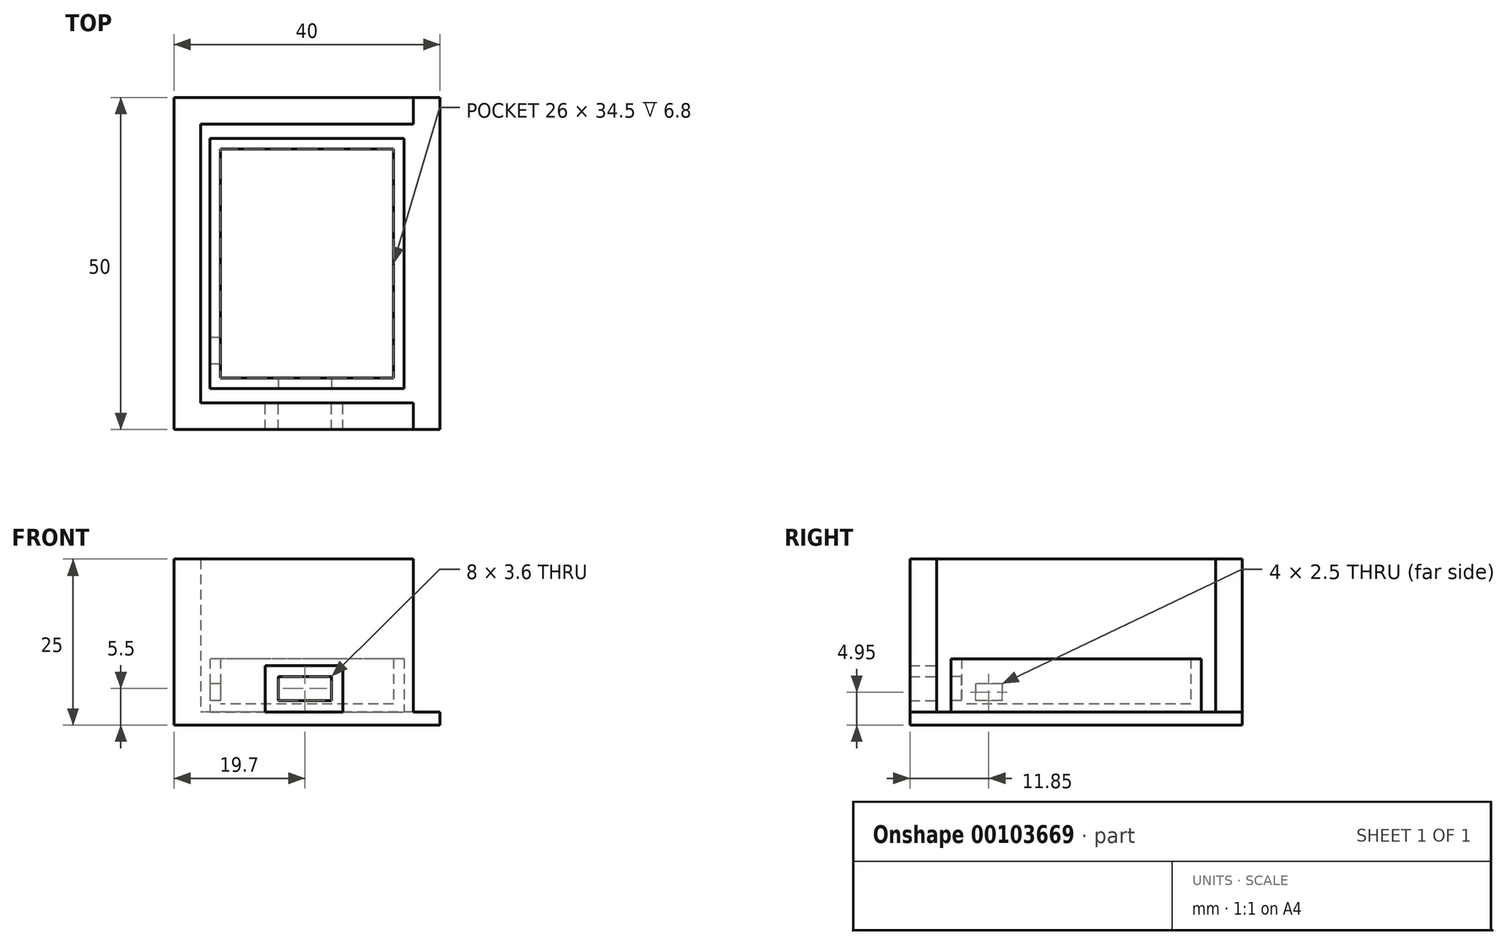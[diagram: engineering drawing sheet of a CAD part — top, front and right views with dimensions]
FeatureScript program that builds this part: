
annotation { "Feature Type Name" : "Feature", "Feature Type Description" : "" }
export const myFeature = defineFeature(function(context is Context, id is Id, definition is map)
    precondition{}
    {
        {
            var Q0;
            Q0=qCreatedBy(makeId("Top.planeOp"),FACE);
            var sketch = newSketch(context, id + "F0", { "sketchPlane" : qUnion([Q0])});
            skLineSegment(sketch, "E0.bottom", {"start": v(14.6, 18.85) * mm, "end": v(-14.6, 18.85) * mm});
            skLineSegment(sketch, "E0.top", {"start": v(14.6, -18.85) * mm, "end": v(-14.6, -18.85) * mm});
            skLineSegment(sketch, "E0.left", {"start": v(14.6, 18.85) * mm, "end": v(14.6, -18.85) * mm});
            skLineSegment(sketch, "E0.right", {"start": v(-14.6, 18.85) * mm, "end": v(-14.6, -18.85) * mm});
            skPoint(sketch, "E0.middle", {"position": v(0, 0) * mm});
            skSolve(sketch);
        }
        {
            var Q0;
            Q0=makeQuery(id+"F0.imprint","IMPRINT",FACE,{"disambiguationData":[TD([[makeQuery(id+"F0.imprint","IMPRINT",EDGE,{"derivedFrom":sQuery(id+"F0.wireOp",EDGE,"E0.bottom")}),1.0]])]});
            extrude(context, id + "F1", {"entities" : qUnion([Q0]), "depth" : 10 * mm});
        }
        {
            var Q0;
            Q0=makeQuery(id+"F1.opExtrude","CAP_FACE",FACE,{"disambiguationData":[OSD([sQuery(id+"F0.wireOp",EDGE,"E0.bottom"),sQuery(id+"F0.wireOp",EDGE,"E0.top"),sQuery(id+"F0.wireOp",EDGE,"E0.left"),sQuery(id+"F0.wireOp",EDGE,"E0.right")])],"isStart":false});
            shell(context, id + "F2", {"entities" : qUnion([Q0]), "thickness" : 1.6 * mm});
        }
        {
            var Q0;
            Q0=makeQuery(id+"F1.opExtrude","SWEPT_FACE",FACE,{"disambiguationData":[OSD([sQuery(id+"F0.wireOp",EDGE,"E0.top")])]});
            var sketch = newSketch(context, id + "F3", { "sketchPlane" : qUnion([Q0])});
            skLineSegment(sketch, "E1.bottom", {"start": v(-4.3, 7.3) * mm, "end": v(3.7, 7.3) * mm});
            skLineSegment(sketch, "E1.top", {"start": v(-4.3, 3.7) * mm, "end": v(3.7, 3.7) * mm});
            skLineSegment(sketch, "E1.left", {"start": v(-4.3, 7.3) * mm, "end": v(-4.3, 3.7) * mm});
            skLineSegment(sketch, "E1.right", {"start": v(3.7, 7.3) * mm, "end": v(3.7, 3.7) * mm});
            skPoint(sketch, "E2.endSnap0", {"position": v(0, 0) * mm});
            skPoint(sketch, "E3", {"position": v(-0.3, 7.3) * mm});
            skLineSegment(sketch, "E4", {"start": v(-2.82, 0) * mm, "end": v(-2.82, 3.7) * mm, "construction": true});
            skLineSegment(sketch, "E5", {"start": v(-4.3, 3.7) * mm, "end": v(-14.6, 3.7) * mm, "construction": true});
            skSolve(sketch);
        }
        {
            var Q0;
            Q0=makeQuery(id+"F3.imprint","IMPRINT",FACE,{"disambiguationData":[TD([[makeQuery(id+"F3.imprint","IMPRINT",EDGE,{"derivedFrom":sQuery(id+"F3.wireOp",EDGE,"E1.bottom")}),-1.0]])]});
            var Q1;
            Q1=makeQuery(id+"F2.opShell","OFFSET_FACE",FACE,{"disambiguationData":[OSD([sQuery(id+"F0.wireOp",EDGE,"E0.top")])]});
            extrude(context, id + "F4", {"entities" : qUnion([Q0]), "operationType" : NewBodyOperationType.REMOVE, "endBound" : BoundingType.UP_TO_SURFACE, "oppositeDirection" : true, "endBoundEntityFace" : qUnion([Q1]), "depth" : 25 * mm});
        }
        {
            var Q0;
            Q0=makeQuery(id+"F1.opExtrude","SWEPT_FACE",FACE,{"disambiguationData":[OSD([sQuery(id+"F0.wireOp",EDGE,"E0.right")])]});
            var sketch = newSketch(context, id + "F5", { "sketchPlane" : qUnion([Q0])});
            skLineSegment(sketch, "E6.bottom", {"start": v(11.15, 6.2) * mm, "end": v(15.15, 6.2) * mm});
            skLineSegment(sketch, "E6.top", {"start": v(11.15, 3.7) * mm, "end": v(15.15, 3.7) * mm});
            skLineSegment(sketch, "E6.left", {"start": v(11.15, 6.2) * mm, "end": v(11.15, 3.7) * mm});
            skLineSegment(sketch, "E6.right", {"start": v(15.15, 6.2) * mm, "end": v(15.15, 3.7) * mm});
            skLineSegment(sketch, "E7", {"start": v(15.15, 3.7) * mm, "end": v(18.85, 3.7) * mm, "construction": true});
            skLineSegment(sketch, "E8", {"start": v(15.15, 3.7) * mm, "end": v(15.15, 0) * mm, "construction": true});
            skSolve(sketch);
        }
        {
            var Q0;
            Q0=makeQuery(id+"F5.imprint","IMPRINT",FACE,{"disambiguationData":[TD([[makeQuery(id+"F5.imprint","IMPRINT",EDGE,{"derivedFrom":sQuery(id+"F5.wireOp",EDGE,"E6.bottom")}),-1.0]])]});
            var Q1;
            Q1=makeQuery(id+"F2.opShell","OFFSET_FACE",FACE,{"disambiguationData":[OSD([sQuery(id+"F0.wireOp",EDGE,"E0.right")])]});
            extrude(context, id + "F6", {"entities" : qUnion([Q0]), "operationType" : NewBodyOperationType.REMOVE, "endBound" : BoundingType.UP_TO_SURFACE, "oppositeDirection" : true, "endBoundEntityFace" : qUnion([Q1]), "depth" : 25 * mm});
        }
        {
            var Q0;
            Q0=makeQuery(id+"F2.opShell","OFFSET_FACE",FACE,{"disambiguationData":[OSD([sQuery(id+"F0.wireOp",EDGE,"E0.bottom"),sQuery(id+"F0.wireOp",EDGE,"E0.top"),sQuery(id+"F0.wireOp",EDGE,"E0.left"),sQuery(id+"F0.wireOp",EDGE,"E0.right")])]});
            var sketch = newSketch(context, id + "F7", { "sketchPlane" : qUnion([Q0])});
            skLineSegment(sketch, "E9.bottom", {"start": v(-13, 17.25) * mm, "end": v(13, 17.25) * mm});
            skLineSegment(sketch, "E9.top", {"start": v(-13, -17.25) * mm, "end": v(13, -17.25) * mm});
            skLineSegment(sketch, "E9.left", {"start": v(-13, 17.25) * mm, "end": v(-13, -17.25) * mm});
            skLineSegment(sketch, "E9.right", {"start": v(13, 17.25) * mm, "end": v(13, -17.25) * mm});
            skSolve(sketch);
        }
        {
            var Q0;
            Q0=makeQuery(id+"F7.imprint","IMPRINT",FACE,{"disambiguationData":[TD([[makeQuery(id+"F7.imprint","IMPRINT",EDGE,{"derivedFrom":sQuery(id+"F7.wireOp",EDGE,"E9.bottom")}),1.0]])]});
            extrude(context, id + "F8", {"entities" : qUnion([Q0]), "operationType" : NewBodyOperationType.ADD, "depth" : 1.6 * mm});
        }
        {
            var Q0;
            Q0=makeQuery(id+"F1.opExtrude","CAP_FACE",FACE,{"disambiguationData":[OSD([sQuery(id+"F0.wireOp",EDGE,"E0.bottom"),sQuery(id+"F0.wireOp",EDGE,"E0.top"),sQuery(id+"F0.wireOp",EDGE,"E0.left"),sQuery(id+"F0.wireOp",EDGE,"E0.right")])],"isStart":true});
            var sketch = newSketch(context, id + "F9", { "sketchPlane" : qUnion([Q0])});
            skLineSegment(sketch, "E10.bottom", {"start": v(-20, -25) * mm, "end": v(20, -25) * mm});
            skLineSegment(sketch, "E10.top", {"start": v(-20, 25) * mm, "end": v(20, 25) * mm});
            skLineSegment(sketch, "E10.left", {"start": v(-20, -25) * mm, "end": v(-20, 25) * mm});
            skLineSegment(sketch, "E10.right", {"start": v(20, -25) * mm, "end": v(20, 25) * mm});
            skPoint(sketch, "E10.middle", {"position": v(0, 0) * mm});
            skLineSegment(sketch, "E11.bottom", {"start": v(20, 25) * mm, "end": v(16, 25) * mm});
            skLineSegment(sketch, "E11.top", {"start": v(20, -25) * mm, "end": v(16, -25) * mm});
            skLineSegment(sketch, "E11.left", {"start": v(20, 25) * mm, "end": v(20, -25) * mm});
            skLineSegment(sketch, "E11.right", {"start": v(16, 25) * mm, "end": v(16, -25) * mm});
            skLineSegment(sketch, "E12.bottom", {"start": v(-20, -25) * mm, "end": v(-16, -25) * mm});
            skLineSegment(sketch, "E12.top", {"start": v(-20, 25) * mm, "end": v(-16, 25) * mm});
            skLineSegment(sketch, "E12.right", {"start": v(-16, -25) * mm, "end": v(-16, 25) * mm});
            skLineSegment(sketch, "E13.top", {"start": v(-20, -21) * mm, "end": v(20, -21) * mm});
            skLineSegment(sketch, "E13.left", {"start": v(-20, -25) * mm, "end": v(-20, -21) * mm});
            skLineSegment(sketch, "E13.right", {"start": v(20, -25) * mm, "end": v(20, -21) * mm});
            skLineSegment(sketch, "E14.top", {"start": v(-20, 21) * mm, "end": v(20, 21) * mm});
            skLineSegment(sketch, "E14.left", {"start": v(-20, 25) * mm, "end": v(-20, 21) * mm});
            skLineSegment(sketch, "E14.right", {"start": v(20, 25) * mm, "end": v(20, 21) * mm});
            skSolve(sketch);
        }
        {
            var Q0;
            {var subQ0=sQuery(id+"F9.wireOp",EDGE,"E10.bottom");var subQ1=sQuery(id+"F9.wireOp",EDGE,"E11.right");var subQ2=makeQuery(id+"F9.imprint","INTERSECT",VERTEX,{"derivedFrom":[subQ1,subQ0]});Q0=makeQuery(id+"F9.imprint","IMPRINT",FACE,{"disambiguationData":[TD([[makeQuery(id+"F9.imprint","IMPRINT",EDGE,{"disambiguationData":[TD([[subQ2,1.0]])],"derivedFrom":subQ1}),-1.0]])]});}
            var Q1;
            {var subQ5=sQuery(id+"F9.wireOp",EDGE,"E13.left");Q1=makeQuery(id+"F9.imprint","IMPRINT",FACE,{"disambiguationData":[TD([[makeQuery(id+"F9.imprint","IMPRINT",EDGE,{"derivedFrom":subQ5}),-1.0]])]});}
            var Q2;
            {var subQ5=sQuery(id+"F9.wireOp",EDGE,"E13.right");Q2=makeQuery(id+"F9.imprint","IMPRINT",FACE,{"disambiguationData":[TD([[makeQuery(id+"F9.imprint","IMPRINT",EDGE,{"derivedFrom":subQ5}),1.0]])]});}
            var Q3;
            {var subQ0=sQuery(id+"F9.wireOp",EDGE,"E11.left");Q3=makeQuery(id+"F9.imprint","IMPRINT",FACE,{"disambiguationData":[TD([[makeQuery(id+"F9.imprint","IMPRINT",EDGE,{"derivedFrom":subQ0}),-1.0]])]});}
            var Q4;
            {var subQ5=sQuery(id+"F9.wireOp",EDGE,"E14.right");Q4=makeQuery(id+"F9.imprint","IMPRINT",FACE,{"disambiguationData":[TD([[makeQuery(id+"F9.imprint","IMPRINT",EDGE,{"derivedFrom":subQ5}),-1.0]])]});}
            var Q5;
            {var subQ0=sQuery(id+"F9.wireOp",EDGE,"E10.top");var subQ1=sQuery(id+"F9.wireOp",EDGE,"E11.right");var subQ2=makeQuery(id+"F9.imprint","INTERSECT",VERTEX,{"derivedFrom":[subQ1,subQ0]});Q5=makeQuery(id+"F9.imprint","IMPRINT",FACE,{"disambiguationData":[TD([[makeQuery(id+"F9.imprint","IMPRINT",EDGE,{"disambiguationData":[TD([[subQ2,-1.0]])],"derivedFrom":subQ1}),-1.0]])]});}
            var Q6;
            {var subQ5=sQuery(id+"F9.wireOp",EDGE,"E14.left");Q6=makeQuery(id+"F9.imprint","IMPRINT",FACE,{"disambiguationData":[TD([[makeQuery(id+"F9.imprint","IMPRINT",EDGE,{"derivedFrom":subQ5}),1.0]])]});}
            var Q7;
            {var subQ0=sQuery(id+"F9.wireOp",EDGE,"E10.left");Q7=makeQuery(id+"F9.imprint","IMPRINT",FACE,{"disambiguationData":[TD([[makeQuery(id+"F9.imprint","IMPRINT",EDGE,{"derivedFrom":subQ0}),-1.0]])]});}
            extrude(context, id + "F10", {"entities" : qUnion([Q0, Q1, Q2, Q3, Q4, Q5, Q6, Q7]), "oppositeDirection" : true, "depth" : 25 * mm});
        }
        {
            var Q0;
            Q0=makeQuery(id+"F10.opExtrude","CAP_FACE",FACE,{"disambiguationData":[OSD([sQuery(id+"F9.wireOp",EDGE,"E11.left"),sQuery(id+"F9.wireOp",EDGE,"E11.right"),sQuery(id+"F9.wireOp",EDGE,"E10.left"),sQuery(id+"F9.wireOp",EDGE,"E12.right"),sQuery(id+"F9.wireOp",EDGE,"E10.bottom"),sQuery(id+"F9.wireOp",EDGE,"E13.top"),sQuery(id+"F9.wireOp",EDGE,"E13.left"),sQuery(id+"F9.wireOp",EDGE,"E13.right"),sQuery(id+"F9.wireOp",EDGE,"E10.top"),sQuery(id+"F9.wireOp",EDGE,"E14.top"),sQuery(id+"F9.wireOp",EDGE,"E14.left"),sQuery(id+"F9.wireOp",EDGE,"E14.right")])],"isStart":true});
            var sketch = newSketch(context, id + "F11", { "sketchPlane" : qUnion([Q0])});
            skLineSegment(sketch, "E15.bottom", {"start": v(-20, 25) * mm, "end": v(20, 25) * mm});
            skLineSegment(sketch, "E15.top", {"start": v(-20, -25) * mm, "end": v(20, -25) * mm});
            skLineSegment(sketch, "E15.left", {"start": v(-20, 25) * mm, "end": v(-20, -25) * mm});
            skLineSegment(sketch, "E15.right", {"start": v(20, 25) * mm, "end": v(20, -25) * mm});
            skSolve(sketch);
        }
        {
            var Q0;
            Q0=makeQuery(id+"F11.imprint","IMPRINT",FACE,{"disambiguationData":[TD([[makeQuery(id+"F11.imprint","IMPRINT",EDGE,{"derivedFrom":sQuery(id+"F11.wireOp",EDGE,"E15.bottom")}),-1.0]])]});
            var Q1;
            Q1=makeQuery(id+"F11.imprint","IMPRINT",FACE,{"disambiguationData":[TD([[makeQuery(id+"F11.imprint","IMPRINT",EDGE,{"derivedFrom":makeQuery(id+"F10.opExtrude","CAP_EDGE",EDGE,{"disambiguationData":[OSD([sQuery(id+"F9.wireOp",EDGE,"E11.right")])],"isStart":true})}),-1.0]])]});
            extrude(context, id + "F12", {"entities" : qUnion([Q0, Q1]), "operationType" : NewBodyOperationType.ADD, "oppositeDirection" : true, "depth" : 2 * mm});
        }
        {
            var Q0;
            Q0=makeQuery(id+"F1.opExtrude","SWEPT_FACE",FACE,{"disambiguationData":[OSD([sQuery(id+"F0.wireOp",EDGE,"E0.top")])]});
            var sketch = newSketch(context, id + "F13", { "sketchPlane" : qUnion([Q0])});
            skLineSegment(sketch, "E16.bottom", {"start": v(-6.32, 8.99) * mm, "end": v(5.42, 8.99) * mm});
            skLineSegment(sketch, "E16.top", {"start": v(-6.32, 1.8) * mm, "end": v(5.42, 1.8) * mm});
            skLineSegment(sketch, "E16.left", {"start": v(-6.32, 8.99) * mm, "end": v(-6.32, 1.8) * mm});
            skLineSegment(sketch, "E16.right", {"start": v(5.42, 8.99) * mm, "end": v(5.42, 1.8) * mm});
            skSolve(sketch);
        }
        {
            var Q0;
            Q0=makeQuery(id+"F13.imprint","IMPRINT",FACE,{"disambiguationData":[TD([[makeQuery(id+"F13.imprint","IMPRINT",EDGE,{"derivedFrom":sQuery(id+"F13.wireOp",EDGE,"E16.bottom")}),-1.0]])]});
            extrude(context, id + "F14", {"entities" : qUnion([Q0]), "operationType" : NewBodyOperationType.REMOVE, "depth" : 25 * mm});
        }
    });
